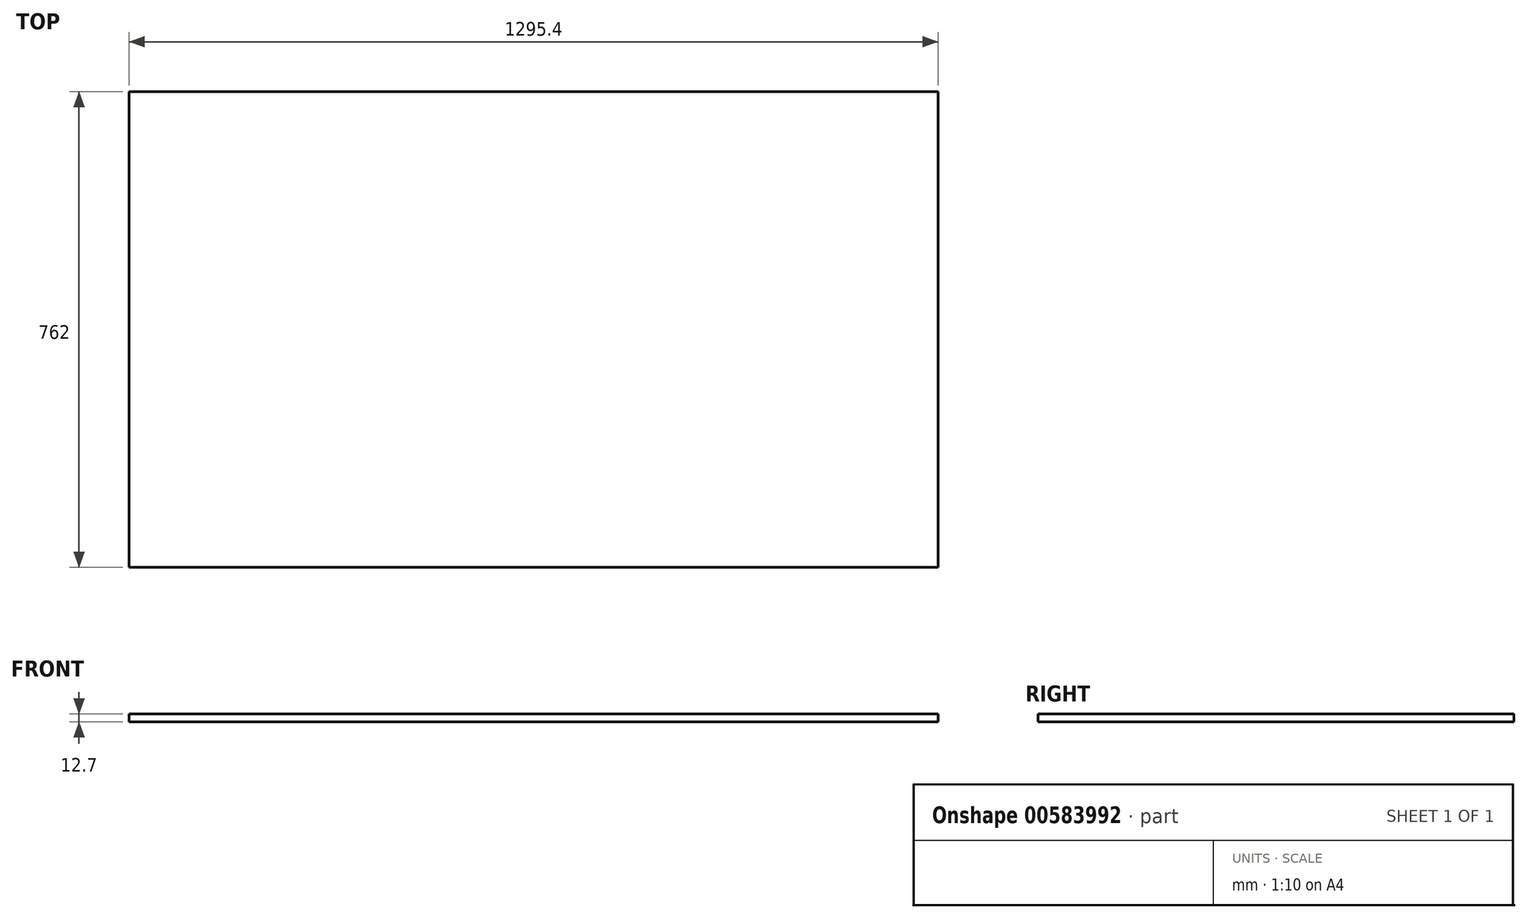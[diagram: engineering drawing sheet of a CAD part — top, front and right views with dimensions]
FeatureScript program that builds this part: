
annotation { "Feature Type Name" : "Feature", "Feature Type Description" : "" }
export const myFeature = defineFeature(function(context is Context, id is Id, definition is map)
    precondition{}
    {
        {
            var Q0;
            Q0=qCreatedBy(makeId("Top.planeOp"),FACE);
            var sketch = newSketch(context, id + "F0", { "sketchPlane" : qUnion([Q0])});
            skLineSegment(sketch, "E0.bottom", {"start": v(-472.4, 396.37) * mm, "end": v(823, 396.37) * mm});
            skLineSegment(sketch, "E0.top", {"start": v(-472.4, -365.63) * mm, "end": v(823, -365.63) * mm});
            skLineSegment(sketch, "E0.left", {"start": v(-472.4, 396.37) * mm, "end": v(-472.4, -365.63) * mm});
            skLineSegment(sketch, "E0.right", {"start": v(823, 396.37) * mm, "end": v(823, -365.63) * mm});
            skSolve(sketch);
        }
        {
            var Q0;
            Q0=qSketchRegion(id+"F0",true);
            extrude(context, id + "F1", {"entities" : qUnion([Q0]), "depth" : 12.7 * mm, "offsetDistance" : 25.4 * mm});
        }
    });
